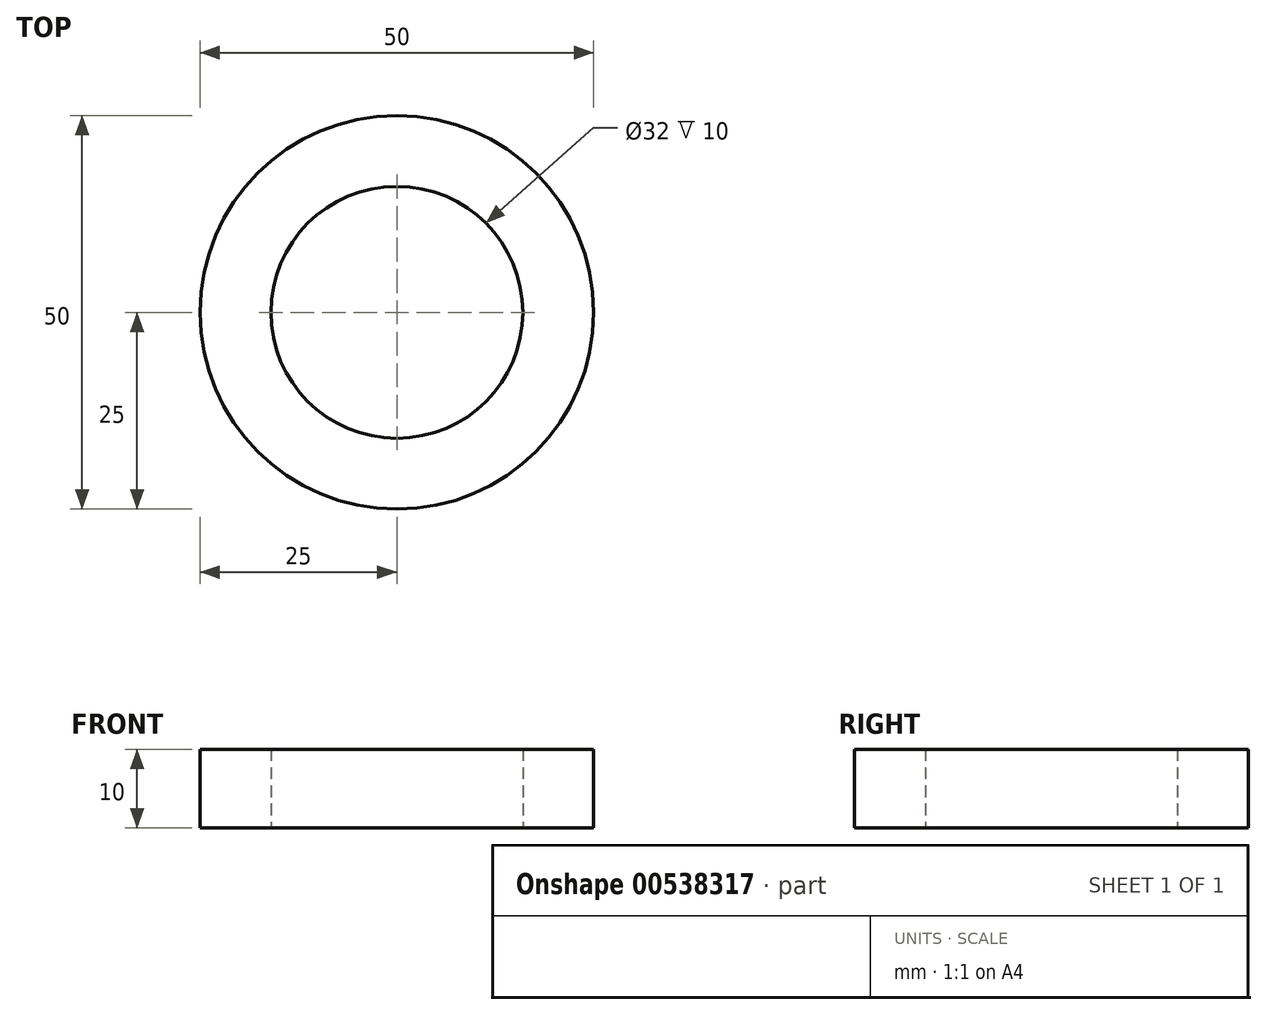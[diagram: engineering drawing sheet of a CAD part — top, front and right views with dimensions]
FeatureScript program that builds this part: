
annotation { "Feature Type Name" : "Feature", "Feature Type Description" : "" }
export const myFeature = defineFeature(function(context is Context, id is Id, definition is map)
    precondition{}
    {
        {
            var Q0;
            Q0=qCreatedBy(makeId("Top.planeOp"),FACE);
            var sketch = newSketch(context, id + "F0", { "sketchPlane" : qUnion([Q0])});
            skCircle(sketch, "E0", {"center": v(0, 0) * mm, "radius": 25 * mm});
            skCircle(sketch, "E1", {"center": v(0, 0) * mm, "radius": 16 * mm});
            skSolve(sketch);
        }
        {
            var Q0;
            Q0 = qSketchRegion(id + "F0", true);
            extrude(context, id + "F1", {"entities" : qUnion([Q0]), "depth" : 10 * mm, "offsetDistance" : 25.4 * mm});
        }
    });
